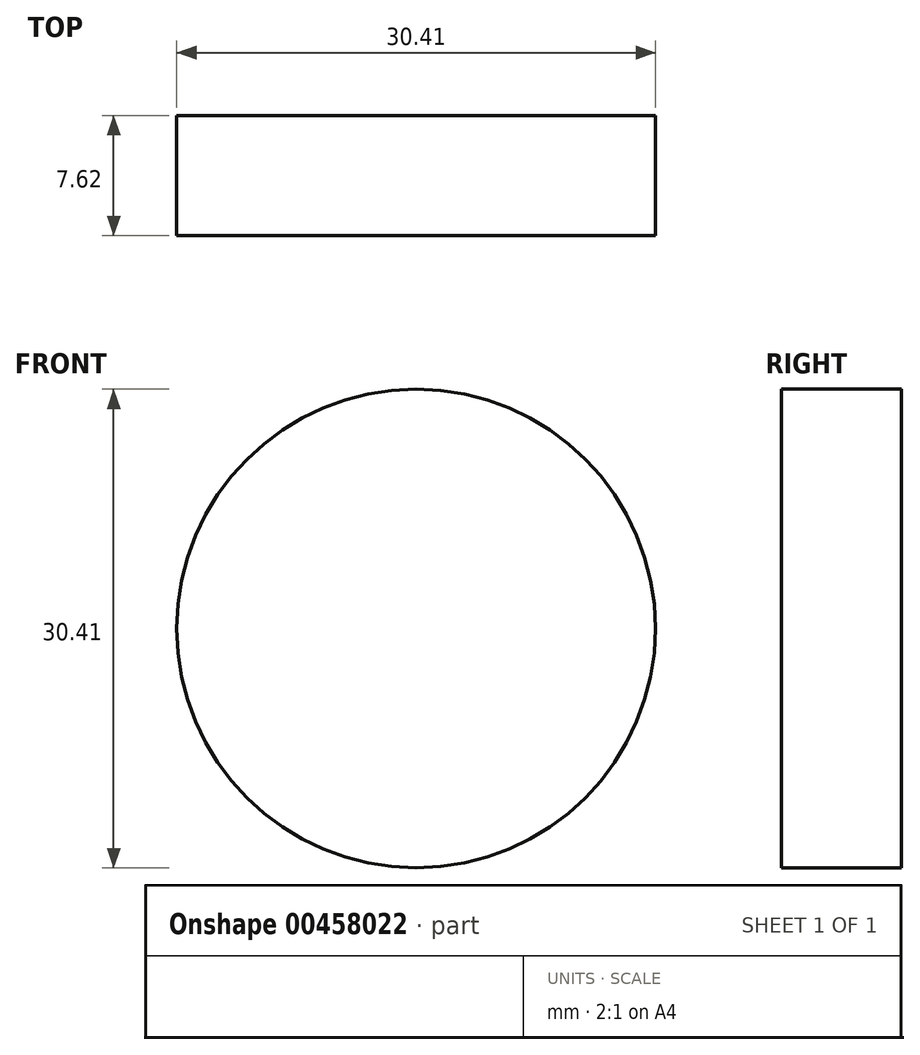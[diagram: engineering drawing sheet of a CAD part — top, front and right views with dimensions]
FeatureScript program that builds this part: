
annotation { "Feature Type Name" : "Feature", "Feature Type Description" : "" }
export const myFeature = defineFeature(function(context is Context, id is Id, definition is map)
    precondition{}
    {
        {
            var Q0;
            Q0=qCreatedBy(makeId("Front.planeOp"),FACE);
            var sketch = newSketch(context, id + "F0", { "sketchPlane" : qUnion([Q0])});
            skCircle(sketch, "E0", {"center": v(-40.52, 29.58) * mm, "radius": 15.2 * mm});
            skSolve(sketch);
        }
        {
            var Q0;
            Q0=makeQuery(id+"F0.imprint","IMPRINT",FACE,{"disambiguationData":[TD([[makeQuery(id+"F0.imprint","IMPRINT",EDGE,{"derivedFrom":sQuery(id+"F0.wireOp",EDGE,"E0")}),1.0]])]});
            extrude(context, id + "F1", {"entities" : qUnion([Q0]), "depth" : 7.62 * mm});
        }
    });
